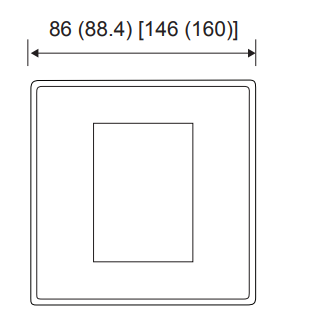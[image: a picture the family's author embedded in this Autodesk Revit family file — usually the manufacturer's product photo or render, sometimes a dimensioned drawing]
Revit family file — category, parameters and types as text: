
# Revit family: Fascia Panel_230D
name_source: partatom
category: Electrical Fixtures
revit_build: Autodesk Revit 2018 (Build: 20170223_1515(x64)
units: mm (PartAtom-declared; Revit-internal decimal feet)

## family parameters
Always vertical = Yes
Cut with Voids When Loaded = No
Maintain Annotation Orientation = No
Part Type = Normal
Room Calculation Point = No
Round Connector Dimension = Use Diameter
Shared = No
Work Plane-Based = Yes

## types (1)
- DG white plastic plate with grid
    Default Elevation = 0 mm  [stored 0 ft]
    Description = RAL 9003 for white
    Double chassis dimension = 146 mm × 86 mm × 5.9 mm
    Double frame dimension = 160 mm × 88.4 mm × 4.5 mm
    Double frame kit -net weight = 144 g
    Manufacturer = Helvar
    Model = 230 D

note: [stored X ft] marks values corroborated as IEEE doubles in the binary element streams (Revit-internal decimal feet)

## geometry (parser evidence)
native form markers: Sweep x8
no freeform markers — native parametric forms only
